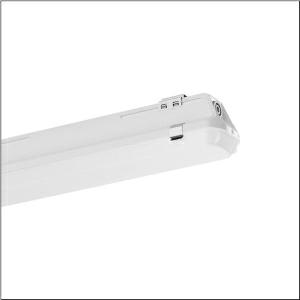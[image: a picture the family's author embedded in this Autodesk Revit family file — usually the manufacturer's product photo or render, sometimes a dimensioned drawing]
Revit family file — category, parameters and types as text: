
# Revit family: monsun_r__11_emergency_51fp10dp467h3h_d298
name_source: partatom
category: Lighting Fixtures
units: mm (PartAtom-declared; Revit-internal decimal feet)

## family parameters
Cut with Voids When Loaded = No
Host = Face
Light Source = No
Part Type = Normal
Room Calculation Point = No
Round Connector Dimension = Use Diameter
Shared = No

## types (1)
- --- (1 x LED, 870 lm, 5 W, 4000K)
    Apparent Load = 5 VA
    CIE Flux Codes = 47 77 93 94 100
    Color Rendering = 80
    Color Temperature = 4000K
    Default Elevation = 1800 mm
    Description = Monsun® 11 emergency, damp-proof luminaire, chain hanger, primary optical cover: enclosure, of PMMA, light emission: direct distribution, primary light characteristic: symmetric, installation type: suspended mounting, surface-mounted, horizontal mounting, vertical mounting, LED, rated luminous flux: 6.050lm, luminous efficacy: 175lm/W, light colour: 840, colour temperature: 4000K, control gear: ECG DALI, with terminal, 5+3-pole, max. 2.5mm², mains connection: 220..240V, AC, 50/60Hz, rated input power: 35W, control gear: single battery element, battery: NiCd, 4,5Ah, mains connection: 230V, 50Hz, luminaire housing, of glass-fibre reinforced polyester, uncoated, bright grey, incl. chain hanger, length: 1.590mm, width: 90mm, height: 88mm, clip for enclosure, of stainless steel (V2A), ceiling mounting element, of stainless steel (V2A), chain hanger, of stainless steel (V2A), protection rating (complete): IP66, insulation class (complete): insulation class I (protective earthing), certification: CE, UKCA, protection symbol: D, impact resistance: IK04, permissible operating ambient temperature: +5..+35°C, standard: EN 50419, EN 60598-2-1, EN 60598-2-22, no direct snow, no direct sun, no direct rain, for indoor or canopied outdoor use, corresponds to IFS (International Featured Standards) requirements for safety and quality in the food industry, contact your sales advisor before using the luminaires in applications with unclear chemical exposure, large temperature fluctuations or condensation-forming humidity, LABS conformity tested according to VDMA 24364:2018-05, packaging unit: 1 piece
    Height = 89 mm
    Lamp = 1 x LED
    Lamp Light Flux = 870 lm
    Lamp Power = 5 W
    Lamp count = 1
    Length = 1590 mm
    Luminous efficacy = 174 lm/W
    Manufacturer = Siteco
    ModVariant = No
    Model = 51FP10DP467H3H
    Mounting Place = Ceiling
    Mounting Type = Surface mounted
    Number of Poles = 1
    OnlyDefault = Yes
    Power Factor = 1
    Product Name = Monsun® 11 emergency
    Product group = damp-proof luminaire
    ProductGroupID = 300
    Protection Class = Protection class I
    Protection Degree = IP 66
    RLX_Detail_Level = 1
    RLX_Emergency_Light_Flux = 0 lm
    RLX_Emergency_Type = 0
    RLX_Emergency_Type_DB = No
    RlxData = <blob elided: 92433 chars, md5=8613978b>
    Socket = socket
    Standby Power = 0 W
    System Light Flux = 870 lm
    System Power = 5 W
    Type Comments = : emergency light operation: 3 h
    Type Image = l_1004748.jpg
    URL = http://relux.com
    VarID = @adj_134669
    Voltage = 0 V
    Weight = 0.00 kg
    Width = 90 mm

## geometry (parser evidence)
native form markers: Blend x4, Sweep x12
no freeform markers — native parametric forms only
